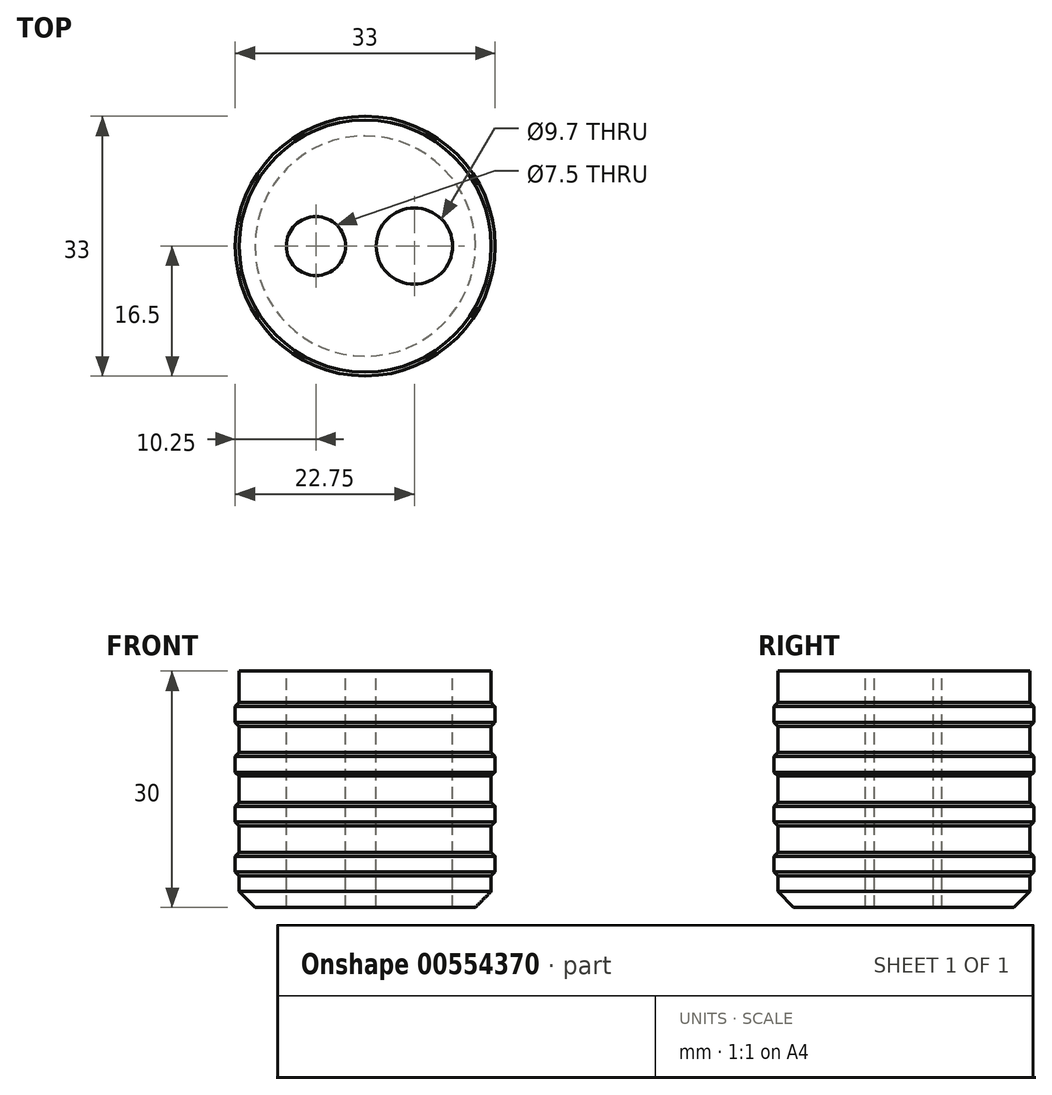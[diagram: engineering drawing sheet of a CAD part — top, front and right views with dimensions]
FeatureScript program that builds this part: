
annotation { "Feature Type Name" : "Feature", "Feature Type Description" : "" }
export const myFeature = defineFeature(function(context is Context, id is Id, definition is map)
    precondition{}
    {
        {
            var Q0;
            Q0=qCreatedBy(makeId("Front.planeOp"),FACE);
            var sketch = newSketch(context, id + "F0", { "sketchPlane" : qUnion([Q0])});
            skLineSegment(sketch, "E0", {"start": v(0, 15) * mm, "end": v(0, -15) * mm});
            skLineSegment(sketch, "E1", {"start": v(0, -15) * mm, "end": v(16, -15) * mm});
            skLineSegment(sketch, "E2", {"start": v(16, -15) * mm, "end": v(16, -11) * mm});
            skLineSegment(sketch, "E3", {"start": v(16, 15) * mm, "end": v(0, 15) * mm});
            skLineSegment(sketch, "E4", {"start": v(16.5, 10.5) * mm, "end": v(16.5, 8.5) * mm});
            skLineSegment(sketch, "E5", {"start": v(16, 11) * mm, "end": v(16.5, 10.5) * mm});
            skLineSegment(sketch, "E6", {"start": v(16.5, 8.5) * mm, "end": v(16, 8) * mm});
            skLineSegment(sketch, "E7.0.1.0", {"start": v(16, 4.67) * mm, "end": v(16.5, 4.17) * mm});
            skLineSegment(sketch, "E7.0.1.1", {"start": v(16.5, 4.17) * mm, "end": v(16.5, 2.17) * mm});
            skLineSegment(sketch, "E7.0.1.2", {"start": v(16.5, 2.17) * mm, "end": v(16, 1.67) * mm});
            skLineSegment(sketch, "E7.0.2.0", {"start": v(16, -1.67) * mm, "end": v(16.5, -2.17) * mm});
            skLineSegment(sketch, "E7.0.2.1", {"start": v(16.5, -2.17) * mm, "end": v(16.5, -4.17) * mm});
            skLineSegment(sketch, "E7.0.2.2", {"start": v(16.5, -4.17) * mm, "end": v(16, -4.67) * mm});
            skLineSegment(sketch, "E7.0.3.0", {"start": v(16, -8) * mm, "end": v(16.5, -8.5) * mm});
            skLineSegment(sketch, "E7.0.3.1", {"start": v(16.5, -8.5) * mm, "end": v(16.5, -10.5) * mm});
            skLineSegment(sketch, "E7.0.3.2", {"start": v(16.5, -10.5) * mm, "end": v(16, -11) * mm});
            skLineSegment(sketch, "E7.direction1", {"start": v(16, 8) * mm, "end": v(24.15, 8) * mm, "construction": true});
            skLineSegment(sketch, "E7.direction2", {"start": v(16, 8) * mm, "end": v(16, 4.67) * mm, "construction": true});
            skLineSegment(sketch, "E8.trimOffspring", {"start": v(16, 11) * mm, "end": v(16, 15) * mm});
            skLineSegment(sketch, "E9.trimOffspring", {"start": v(16, -1.67) * mm, "end": v(16, 1.67) * mm});
            skLineSegment(sketch, "E10.trimOffspring", {"start": v(16, -8) * mm, "end": v(16, -4.67) * mm});
            skLineSegment(sketch, "E11.trimOffspring", {"start": v(16, 4.67) * mm, "end": v(16, 8) * mm});
            skLineSegment(sketch, "E12", {"start": v(0, 0) * mm, "end": v(16, 0) * mm, "construction": true});
            skSolve(sketch);
        }
        {
            var Q0;
            Q0 = qSketchRegion(id + "F0", true);
            var Q1;
            Q1=sQuery(id+"F0.wireOp",EDGE,"E0");
            revolve(context, id + "F1", {"entities" : qUnion([Q0]), "axis" : qUnion([Q1]), "revolveType" : RevolveType.FULL});
        }
        {
            var Q0;
            Q0=makeQuery(id+"F1.opRevolve","SWEPT_FACE",FACE,{"disambiguationData":[OSD([sQuery(id+"F0.wireOp",EDGE,"E3")])]});
            var sketch = newSketch(context, id + "F2", { "sketchPlane" : qUnion([Q0])});
            skLineSegment(sketch, "E13", {"start": v(-6.25, 0) * mm, "end": v(6.25, 0) * mm, "construction": true});
            skCircle(sketch, "E14", {"center": v(-6.25, 0) * mm, "radius": 3.75 * mm});
            skCircle(sketch, "E15", {"center": v(6.25, 0) * mm, "radius": 4.85 * mm});
            skSolve(sketch);
        }
        {
            var Q0;
            Q0 = qSketchRegion(id + "F2", true);
            extrude(context, id + "F3", {"entities" : qUnion([Q0]), "operationType" : NewBodyOperationType.REMOVE, "endBound" : BoundingType.THROUGH_ALL, "oppositeDirection" : true, "depth" : 25 * mm, "offsetDistance" : 25 * mm});
        }
        {
            var Q0;
            Q0=makeQuery(id+"F1.opRevolve","SWEPT_EDGE",EDGE,{"disambiguationData":[OSD([sQuery(id+"F0.wireOp",EDGE,"E1"),sQuery(id+"F0.wireOp",EDGE,"E2")])]});
            chamfer(context, id + "F4", {"entities" : qUnion([Q0]), "width" : 2 * mm, "tangentPropagation" : true});
        }
    });
